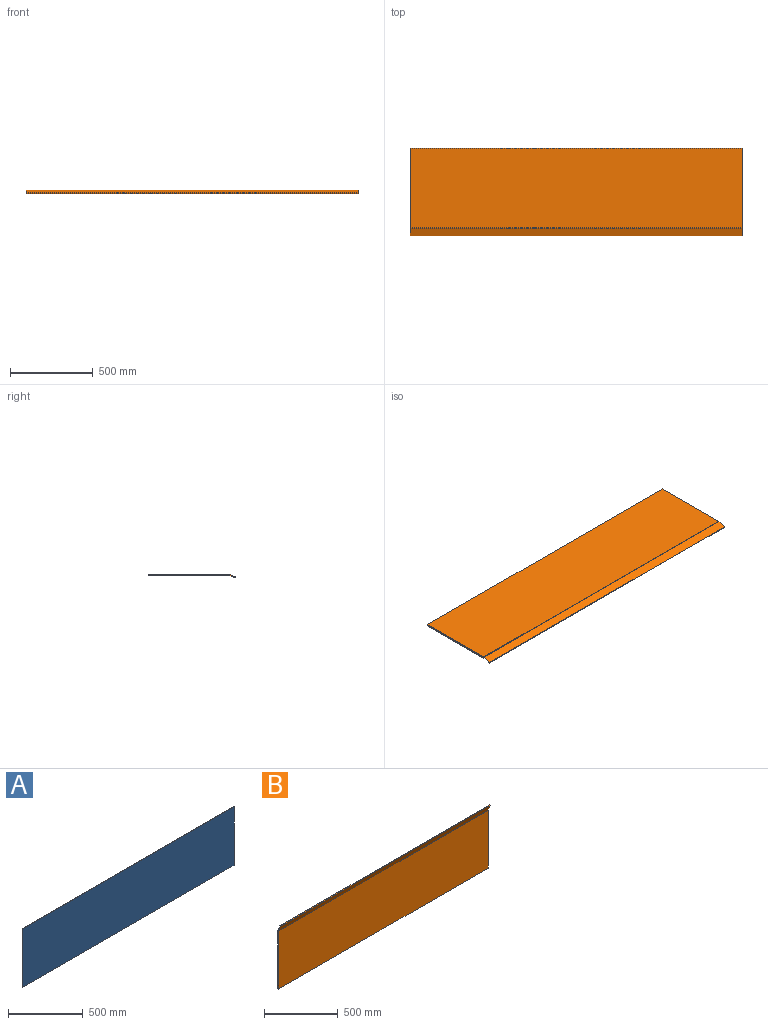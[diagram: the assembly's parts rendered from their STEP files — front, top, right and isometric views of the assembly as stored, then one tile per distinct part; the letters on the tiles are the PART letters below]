
ASSEMBLY  parts=2 mates=1
PART A: 6 faces, bbox 2005x5x480 mm
  f0: plane 2005x5mm, normal (0,0,-1), area 10025mm2, adj f1,f3,f4,f5
  f1: plane 480x5mm, normal (1,0,0), area 2400mm2, adj f0,f2,f4,f5
  f2: plane 2005x5mm, normal (0,0,1), area 10025mm2, adj f1,f3,f4,f5
  f3: plane 480x5mm, normal (-1,0,0), area 2400mm2, adj f0,f2,f4,f5
  f4: plane 2005x480mm, normal (0,-1,0), area 962400mm2, adj f0,f1,f2,f3
  f5: plane 2005x480mm, normal (0,1,0), area 962400mm2, adj f0,f1,f2,f3
PART B: 14 faces, bbox 2005x22.7x528 mm
  f0: plane 479.65x6mm, normal (1,0,0), area 2877.9mm2, adj f1,f3,f4,f10
  f1: plane 2005x6mm, normal (0,0,-1), area 12030mm2, adj f0,f2,f3,f4
  f2: plane 479.65x6mm, normal (-1,0,0), area 2877.9mm2, adj f1,f3,f4,f11
  f3: plane 2005x479.65mm, normal (0,1,0), area 961692.9mm2, adj f0,f1,f2,f12
  f4: plane 2005x479.65mm, normal (0,-1,0), area 961692.9mm2, adj f0,f1,f2,f13
  f5: plane 47.71x22.26mm, normal (1,0,0), area 291.5mm2, adj f7,f8,f9,f10
  f6: plane 47.71x22.26mm, normal (-1,0,0), area 291.5mm2, adj f7,f8,f9,f11
  f7: plane 2005x5.64mm, normal (0,-0.34,0.94), area 12030mm2, adj f5,f6,f8,f9
  f8: plane 2005x45.66mm, normal (0,0.94,0.34), area 97421.7mm2, adj f5,f6,f7,f12
  f9: plane 2005x45.66mm, normal (0,-0.94,-0.34), area 97421.7mm2, adj f5,f6,f7,f13
  f10: plane 6.12x2.74mm, normal (1,0,0), area 10.5mm2, adj f0,f5,f12,f13
  f11: plane 6.12x2.74mm, normal (-1,0,0), area 10.5mm2, adj f2,f6,f12,f13
  f12: cylinder r=8mm len=2005mm, axis (1,0,0), area 5599mm2, adj f3,f8,f10,f11
  f13: cylinder r=2mm len=2005mm, axis (1,0,0), area 1399.8mm2, adj f4,f9,f10,f11
PLACE A rot(axis=(-1,0,0),90deg) t=(-12.41,217.28,205.32)mm
PLACE B rot(axis=(1,0,0),90deg) t=(-12.41,217.28,213.82)mm
MATE fastened A.f4 <-> B.f4  axis (0,0,1) through (990.09,457.28,207.82)mm
